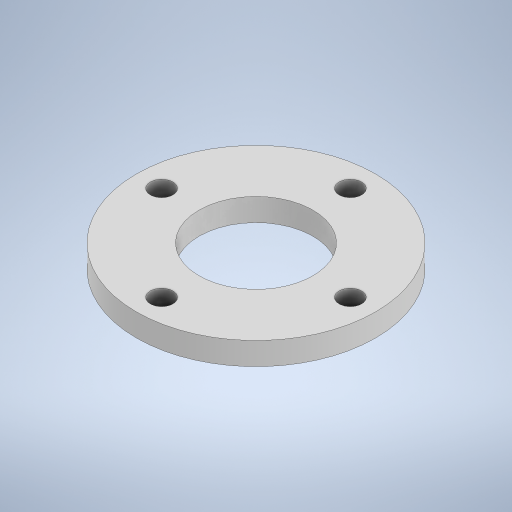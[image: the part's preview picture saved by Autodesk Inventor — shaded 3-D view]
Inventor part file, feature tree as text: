
AUTODESK INVENTOR PART (.ipt)
format: ipt  version: 2023 (Build 270158000, 158)  size: 235,520 bytes
history: native  units: mm
features: extrude x1, sketch x1
ambient origin geometry x8: Origin, YZ Plane, XZ Plane, XY Plane, X Axis, Y Axis, Z Axis, Center Point
bodies: Solido1 (feature_tree)
feature tree (2):
  extrude  "Estrusione1"  Depth=190.0mm
  sketch  "Schizzo1"
